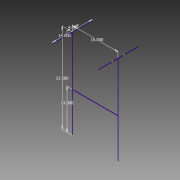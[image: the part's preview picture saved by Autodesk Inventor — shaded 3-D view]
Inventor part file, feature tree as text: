
AUTODESK INVENTOR PART (.ipt)
format: ipt  version: 2013 (Build 170138000, 138)  size: 68,608 bytes
history: native  units: in
note: dims shown in document units (in); Inventor stores cm internally (conversion verified against a paired STEP export)
features: sketch x3, plane x2
ambient origin geometry x8: Origin, YZ Plane, XZ Plane, XY Plane, X Axis, Y Axis, Z Axis, Center Point
feature tree (5):
  sketch  "Sketch1"  dims[d0=31.5in]
  plane  "Work Plane1"
  sketch  "Sketch3"  dims[d2=16.0in]
  plane  "Work Plane2"
  sketch  "Sketch4"  dims[d3=14.0in d4=14.0in d6=4.0in]
